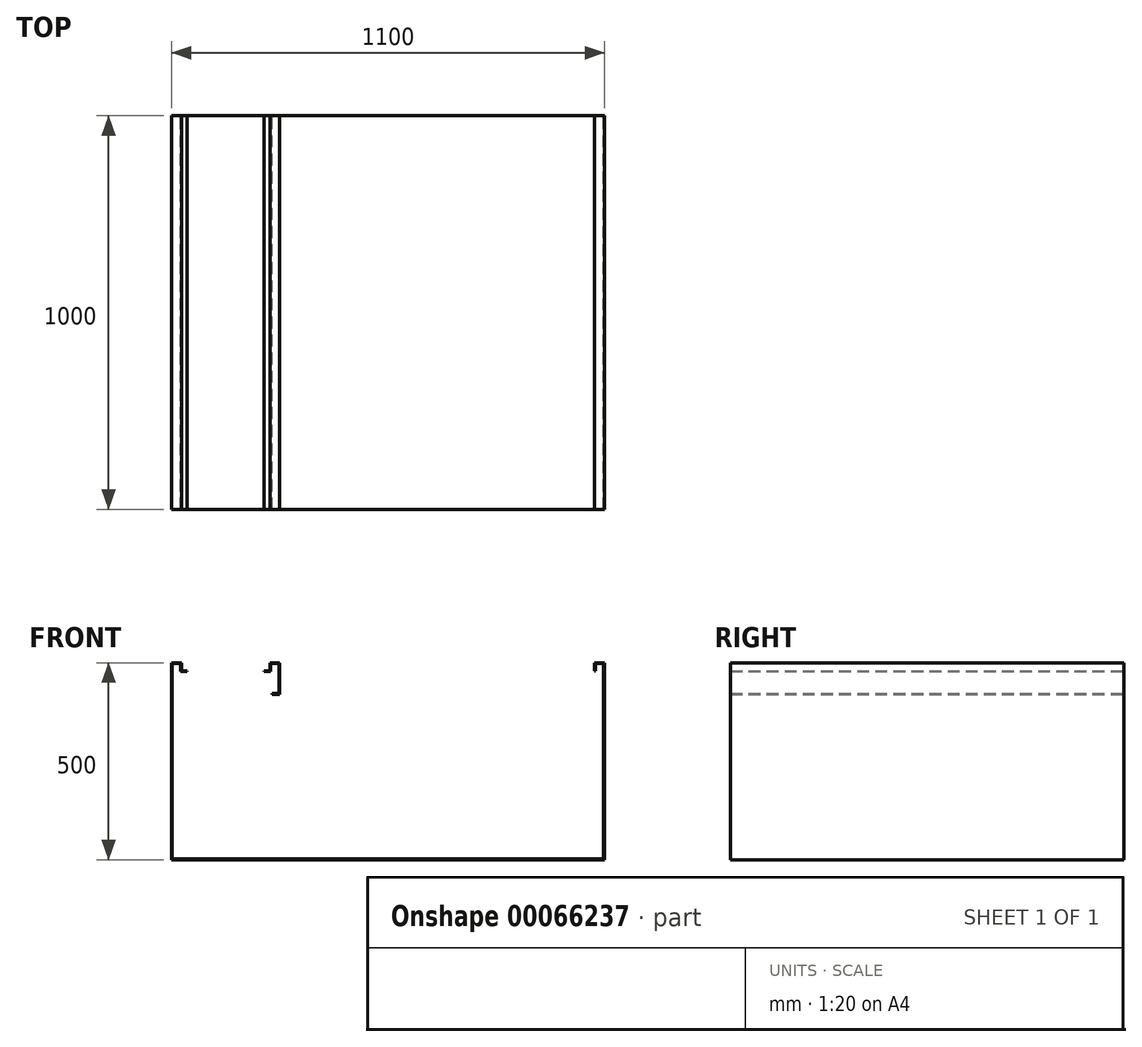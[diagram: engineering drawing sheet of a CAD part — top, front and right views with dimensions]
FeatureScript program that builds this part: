
annotation { "Feature Type Name" : "Feature", "Feature Type Description" : "" }
export const myFeature = defineFeature(function(context is Context, id is Id, definition is map)
    precondition{}
    {
        {
            var Q0;
            Q0=qCreatedBy(makeId("Front.planeOp"),FACE);
            var sketch = newSketch(context, id + "F0", { "sketchPlane" : qUnion([Q0])});
            skLineSegment(sketch, "E0", {"start": v(-35.52, 413.35) * mm, "end": v(-50.52, 413.35) * mm});
            skLineSegment(sketch, "E1", {"start": v(-50.52, 413.35) * mm, "end": v(-50.52, 433.35) * mm});
            skLineSegment(sketch, "E2", {"start": v(-50.52, 433.35) * mm, "end": v(-75.52, 433.35) * mm});
            skLineSegment(sketch, "E3", {"start": v(-75.52, 433.35) * mm, "end": v(-75.52, -66.65) * mm});
            skLineSegment(sketch, "E4", {"start": v(-75.52, -66.65) * mm, "end": v(1024.48, -66.65) * mm});
            skLineSegment(sketch, "E5", {"start": v(1024.48, -66.65) * mm, "end": v(1024.48, 433.35) * mm});
            skLineSegment(sketch, "E6", {"start": v(1024.48, 433.35) * mm, "end": v(999.48, 433.35) * mm});
            skLineSegment(sketch, "E7", {"start": v(999.48, 433.35) * mm, "end": v(999.48, 413.35) * mm});
            skLineSegment(sketch, "E8", {"start": v(199.48, 433.35) * mm, "end": v(199.48, 353.35) * mm});
            skLineSegment(sketch, "E9", {"start": v(199.48, 353.35) * mm, "end": v(179.48, 353.35) * mm});
            skLineSegment(sketch, "E10", {"start": v(199.48, 433.35) * mm, "end": v(174.48, 433.35) * mm});
            skLineSegment(sketch, "E11", {"start": v(174.48, 433.35) * mm, "end": v(174.48, 413.35) * mm});
            skLineSegment(sketch, "E12", {"start": v(174.48, 413.35) * mm, "end": v(159.48, 413.35) * mm});
            skLineSegment(sketch, "E13.0", {"start": v(-35.52, 411.35) * mm, "end": v(-50.52, 411.35) * mm});
            skLineSegment(sketch, "E14.0", {"start": v(-52.52, 411.35) * mm, "end": v(-52.52, 433.35) * mm});
            skLineSegment(sketch, "E15.0", {"start": v(-50.52, 431.35) * mm, "end": v(-75.52, 431.35) * mm});
            skLineSegment(sketch, "E16.0", {"start": v(-73.52, 433.35) * mm, "end": v(-73.52, -66.65) * mm});
            skLineSegment(sketch, "E17.0", {"start": v(-75.52, -64.65) * mm, "end": v(1024.48, -64.65) * mm});
            skLineSegment(sketch, "E18.0", {"start": v(1022.48, -66.65) * mm, "end": v(1022.48, 433.35) * mm});
            skLineSegment(sketch, "E19.0", {"start": v(1024.48, 431.35) * mm, "end": v(999.48, 431.35) * mm});
            skLineSegment(sketch, "E20.0", {"start": v(1001.48, 433.35) * mm, "end": v(1001.48, 413.35) * mm});
            skLineSegment(sketch, "E21.0", {"start": v(176.48, 411.35) * mm, "end": v(159.48, 411.35) * mm});
            skLineSegment(sketch, "E22.0", {"start": v(176.48, 433.35) * mm, "end": v(176.48, 411.35) * mm});
            skLineSegment(sketch, "E23.0", {"start": v(199.48, 431.35) * mm, "end": v(174.48, 431.35) * mm});
            skLineSegment(sketch, "E24.0", {"start": v(197.48, 433.35) * mm, "end": v(197.48, 353.35) * mm});
            skLineSegment(sketch, "E25.0", {"start": v(199.48, 355.35) * mm, "end": v(179.48, 355.35) * mm});
            skLineSegment(sketch, "E26", {"start": v(-35.52, 411.35) * mm, "end": v(-35.52, 413.35) * mm});
            skLineSegment(sketch, "E27", {"start": v(159.48, 411.35) * mm, "end": v(159.48, 413.35) * mm});
            skLineSegment(sketch, "E28", {"start": v(179.48, 353.35) * mm, "end": v(179.48, 355.35) * mm});
            skLineSegment(sketch, "E29", {"start": v(999.48, 413.35) * mm, "end": v(1001.48, 413.35) * mm});
            skLineSegment(sketch, "E30", {"start": v(-50.52, 411.35) * mm, "end": v(-52.52, 411.35) * mm});
            skSolve(sketch);
        }
        {
            var Q0;
            Q0 = qSketchRegion(id + "F0", true);
            extrude(context, id + "F1", {"entities" : qUnion([Q0]), "depth" : 1000 * mm});
        }
    });
